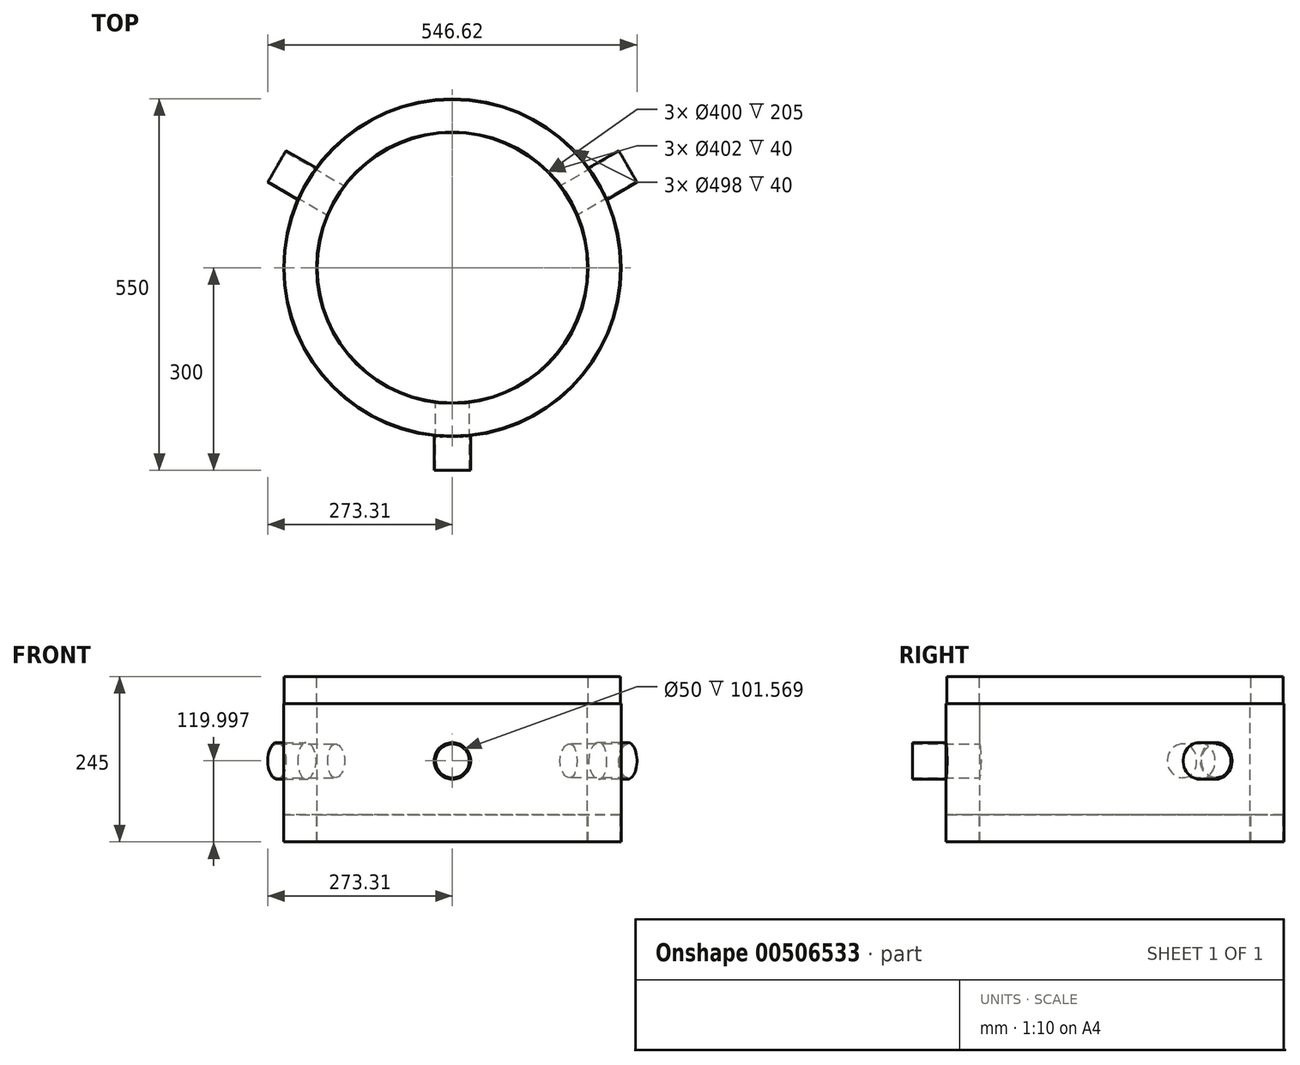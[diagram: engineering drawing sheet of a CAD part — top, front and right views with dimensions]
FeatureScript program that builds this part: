
annotation { "Feature Type Name" : "Feature", "Feature Type Description" : "" }
export const myFeature = defineFeature(function(context is Context, id is Id, definition is map)
    precondition{}
    {
        {
            var Q0;
            Q0=qCreatedBy(makeId("Front.planeOp"),FACE);
            var sketch = newSketch(context, id + "F0", { "sketchPlane" : qUnion([Q0])});
            skLineSegment(sketch, "E0", {"start": v(0, 74.87) * mm, "end": v(0, -73.71) * mm, "construction": true});
            skLineSegment(sketch, "E1", {"start": v(0, 374.84) * mm, "end": v(0, -528.94) * mm, "construction": true});
            skLineSegment(sketch, "E2", {"start": v(-200, -489.75) * mm, "end": v(-200, -284.75) * mm});
            skLineSegment(sketch, "E3", {"start": v(-200, -284.75) * mm, "end": v(-201, -284.75) * mm});
            skLineSegment(sketch, "E4", {"start": v(-201, -284.75) * mm, "end": v(-201, -244.75) * mm});
            skLineSegment(sketch, "E5", {"start": v(-201, -244.75) * mm, "end": v(-249, -244.75) * mm});
            skLineSegment(sketch, "E6", {"start": v(-249, -244.75) * mm, "end": v(-249, -284.75) * mm});
            skLineSegment(sketch, "E7", {"start": v(-249, -284.75) * mm, "end": v(-250, -284.75) * mm});
            skLineSegment(sketch, "E8", {"start": v(-250, -284.75) * mm, "end": v(-250, -489.75) * mm});
            skLineSegment(sketch, "E9", {"start": v(-250, -489.75) * mm, "end": v(-249, -489.75) * mm});
            skLineSegment(sketch, "E10", {"start": v(-249, -489.75) * mm, "end": v(-249, -449.75) * mm});
            skLineSegment(sketch, "E11", {"start": v(-249, -449.75) * mm, "end": v(-201, -449.75) * mm});
            skLineSegment(sketch, "E12", {"start": v(-201, -449.75) * mm, "end": v(-201, -489.75) * mm});
            skLineSegment(sketch, "E13", {"start": v(-201, -489.75) * mm, "end": v(-200, -489.75) * mm});
            skSolve(sketch);
        }
        {
            var Q0;
            Q0=qSketchRegion(id+"F0",true);
            var Q1;
            Q1=sQuery(id+"F0.wireOp",EDGE,"E1");
            revolve(context, id + "F1", {"entities" : qUnion([Q0]), "axis" : qUnion([Q1]), "revolveType" : RevolveType.FULL});
        }
        {
            var Q0;
            Q0=qCreatedBy(makeId("Front.planeOp"),FACE);
            var sketch = newSketch(context, id + "F2", { "sketchPlane" : qUnion([Q0])});
            skLineSegment(sketch, "E14", {"start": v(0, 0) * mm, "end": v(0, -739.5) * mm, "construction": true});
            skCircle(sketch, "E15", {"center": v(0, -369.75) * mm, "radius": 25 * mm});
            skLineSegment(sketch, "E16.0", {"start": v(-249, -244.75) * mm, "end": v(249, -244.75) * mm, "construction": true});
            skSolve(sketch);
        }
        {
            var Q0;
            Q0=qSketchRegion(id+"F2",true);
            extrude(context, id + "F3", {"entities" : qUnion([Q0]), "operationType" : NewBodyOperationType.REMOVE, "depth" : 661 * mm});
        }
        {
            var Q0;
            Q0=qCreatedBy(makeId("Front.planeOp"),FACE);
            cPlane(context, id + "F4", {"entities" : qUnion([Q0]), "cplaneType" : CPlaneType.OFFSET, "offset" : 250 * mm, "width" : 150 * mm, "height" : 150 * mm});
        }
        {
            var Q0;
            Q0=qCreatedBy(id+"F4.planeOp",FACE);
            var sketch = newSketch(context, id + "F5", { "sketchPlane" : qUnion([Q0])});
            skLineSegment(sketch, "E17", {"start": v(0, 0) * mm, "end": v(0, -620.93) * mm, "construction": true});
            skLineSegment(sketch, "E18.0", {"start": v(-249, -244.75) * mm, "end": v(249, -244.75) * mm, "construction": true});
            skCircle(sketch, "E19.0", {"center": v(0, -369.75) * mm, "radius": 25 * mm});
            skCircle(sketch, "E20", {"center": v(0, -369.75) * mm, "radius": 27 * mm});
            skSolve(sketch);
        }
        {
            var Q0;
            Q0=qSketchRegion(id+"F5",true);
            extrude(context, id + "F6", {"entities" : qUnion([Q0]), "operationType" : NewBodyOperationType.ADD, "endBound" : BoundingType.SYMMETRIC, "depth" : 100 * mm, "offsetDistance" : 25 * mm});
        }
        {
            var Q0;
            Q0=makeQuery(id+"F1.opRevolve","SWEPT_BODY",BODY,{"disambiguationData":[OSD([sQuery(id+"F0.wireOp",EDGE,"E2"),sQuery(id+"F0.wireOp",EDGE,"E3"),sQuery(id+"F0.wireOp",EDGE,"E4"),sQuery(id+"F0.wireOp",EDGE,"E5"),sQuery(id+"F0.wireOp",EDGE,"E6"),sQuery(id+"F0.wireOp",EDGE,"E7"),sQuery(id+"F0.wireOp",EDGE,"E8"),sQuery(id+"F0.wireOp",EDGE,"E9"),sQuery(id+"F0.wireOp",EDGE,"E10"),sQuery(id+"F0.wireOp",EDGE,"E11"),sQuery(id+"F0.wireOp",EDGE,"E12"),sQuery(id+"F0.wireOp",EDGE,"E13")])]});
            var Q1;
            Q1=sQuery(id+"F2.wireOp",EDGE,"E14");
            circularPattern(context, id + "F7", {"entities" : qUnion([Q0]), "axis" : qUnion([Q1]), "angle" : 360 * degree, "instanceCount" : 3, "equalSpace" : true});
        }
    });
